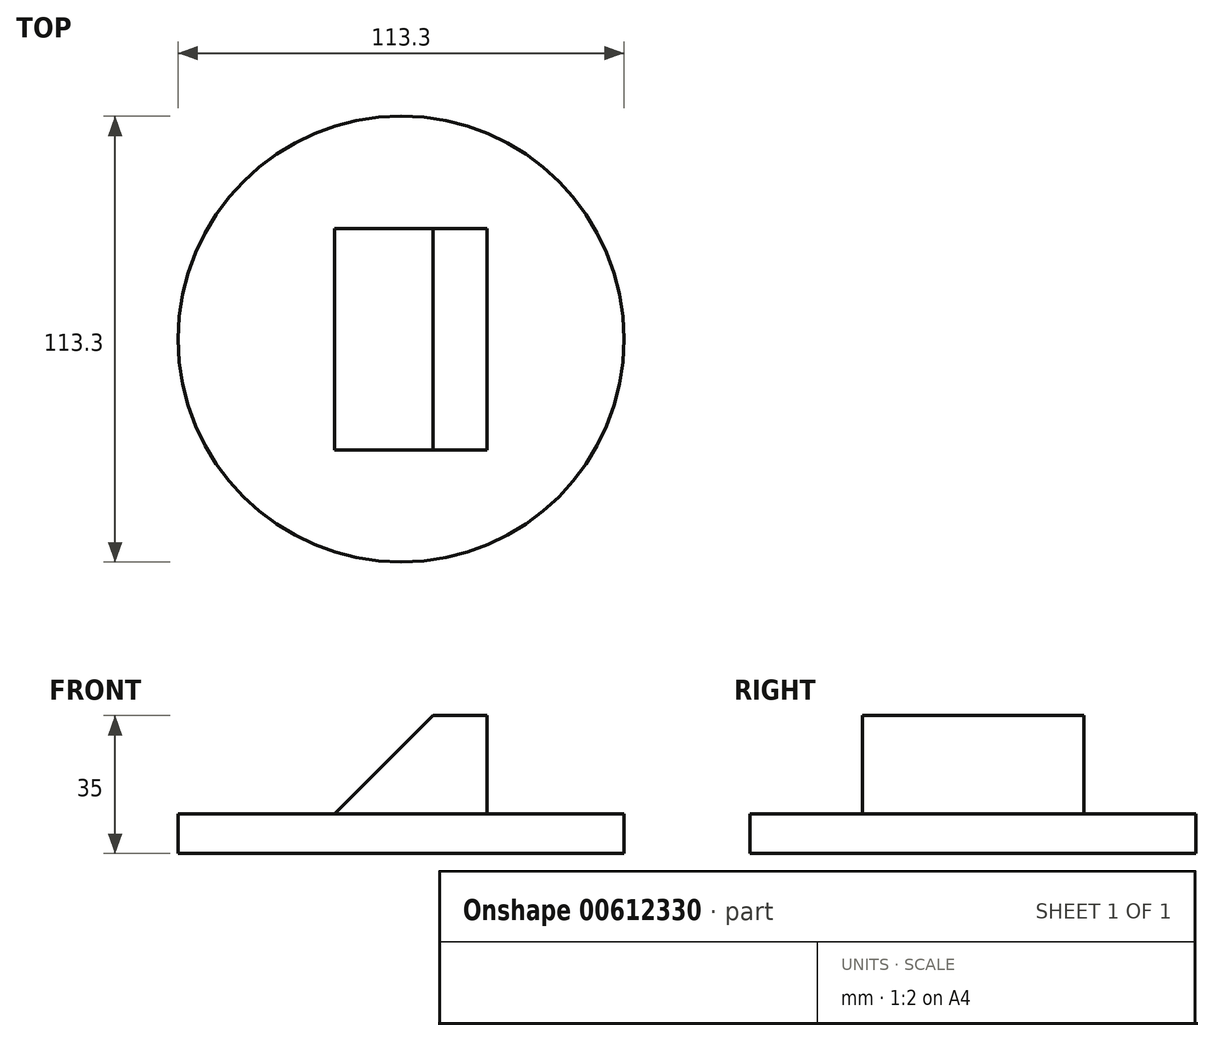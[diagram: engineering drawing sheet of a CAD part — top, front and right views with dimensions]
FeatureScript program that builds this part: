
annotation { "Feature Type Name" : "Feature", "Feature Type Description" : "" }
export const myFeature = defineFeature(function(context is Context, id is Id, definition is map)
    precondition{}
    {
        {
            var Q0;
            Q0=qCreatedBy(makeId("Top.planeOp"),FACE);
            var sketch = newSketch(context, id + "F0", { "sketchPlane" : qUnion([Q0])});
            skCircle(sketch, "E0", {"center": v(0, 0) * mm, "radius": 56.65 * mm});
            skSolve(sketch);
        }
        {
            var Q0;
            Q0=makeQuery(id+"F0.imprint","IMPRINT",FACE,{"disambiguationData":[TD([[makeQuery(id+"F0.imprint","IMPRINT",EDGE,{"derivedFrom":sQuery(id+"F0.wireOp",EDGE,"E0")}),1.0]])]});
            extrude(context, id + "F1", {"entities" : qUnion([Q0]), "depth" : 10 * mm, "offsetDistance" : 25 * mm});
        }
        {
            var Q0;
            Q0=makeQuery(id+"F1.opExtrude","CAP_FACE",FACE,{"disambiguationData":[OSD([sQuery(id+"F0.wireOp",EDGE,"E0")])],"isStart":false});
            var sketch = newSketch(context, id + "F2", { "sketchPlane" : qUnion([Q0])});
            skLineSegment(sketch, "E1.bottom", {"start": v(21.85, 28.15) * mm, "end": v(-21.85, 28.15) * mm});
            skLineSegment(sketch, "E1.top", {"start": v(21.85, -28.15) * mm, "end": v(-21.85, -28.15) * mm});
            skLineSegment(sketch, "E1.left", {"start": v(21.85, 28.15) * mm, "end": v(21.85, -28.15) * mm});
            skLineSegment(sketch, "E1.right", {"start": v(-21.85, 28.15) * mm, "end": v(-21.85, -28.15) * mm});
            skPoint(sketch, "E1.middle", {"position": v(0, 0) * mm});
            skSolve(sketch);
        }
        {
            var Q0;
            Q0=makeQuery(id+"F2.imprint","IMPRINT",FACE,{"disambiguationData":[TD([[makeQuery(id+"F2.imprint","IMPRINT",EDGE,{"derivedFrom":sQuery(id+"F2.wireOp",EDGE,"E1.bottom")}),1.0]])]});
            extrude(context, id + "F3", {"entities" : qUnion([Q0]), "operationType" : NewBodyOperationType.ADD, "depth" : 25 * mm, "offsetDistance" : 25 * mm});
        }
        {
            var Q0;
            Q0=makeQuery(id+"F3.opExtrude","CAP_EDGE",EDGE,{"disambiguationData":[OSD([sQuery(id+"F2.wireOp",EDGE,"E1.right")])],"isStart":false});
            chamfer(context, id + "F4", {"entities" : qUnion([Q0]), "width" : 30 * mm, "tangentPropagation" : true});
        }
    });
